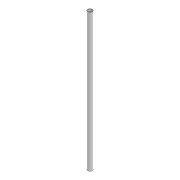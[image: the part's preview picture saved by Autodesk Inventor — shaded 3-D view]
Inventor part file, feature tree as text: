
AUTODESK INVENTOR PART (.ipt)
format: ipt  version: 2022 (Build 260153000, 153)  size: 77,824 bytes
history: native  units: mm
features: extrude x1, sketch x1
ambient origin geometry x8: Origin, YZ Plane, XZ Plane, XY Plane, X Axis, Y Axis, Z Axis, Center Point
bodies: Solid1 (feature_tree)
feature tree (2):
  extrude  "Extrusion1"  Depth=1260.0mm
  sketch  "Sketch1"  dims[d0=40.0mm d1=3.0mm d2=1260.0mm d3=0.0mm]
